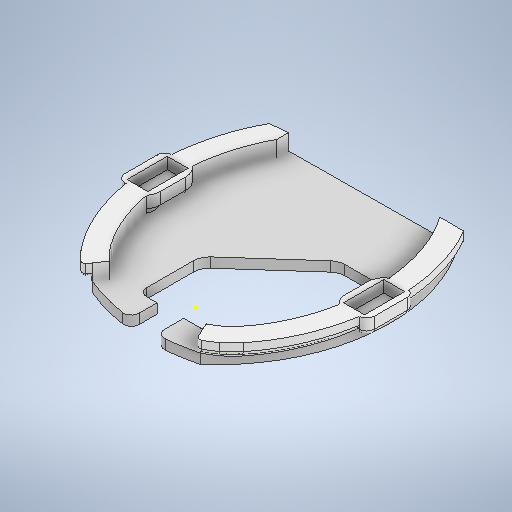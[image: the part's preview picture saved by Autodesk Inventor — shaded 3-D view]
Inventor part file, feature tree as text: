
AUTODESK INVENTOR PART (.ipt)
format: ipt  version: 2025.2 (Build 292293000, 293)  size: 827,392 bytes
history: native  units: in
note: dims shown in document units (in); Inventor stores cm internally (conversion verified against a paired STEP export)
features: fillet x10, sketch x6, extrude x5, other x3
ambient origin geometry x8: Origin, YZ Plane, XZ Plane, XY Plane, X Axis, Y Axis, Z Axis, Center Point
bodies: Solid1 (feature_tree), Solid2 (feature_tree)
feature tree (24):
  other  "rat_cap_EC_v12.iam"
  other  "rat_cap_walls_v8.iam:1::rat_cap_left_wall_v8.ipt:1"
  other  "rat_cap_walls_v8.iam:1::rat_cap_right_wall_v8.ipt:1"
  extrude  "Extrusion1"  Depth=0.3937in TaperAngle=0.0deg
  sketch  "Sketch3"  dims[d16=0.315in d17=0.0812in d18=0.0in]
  extrude  "Extrusion4"  Depth=0.0812in TaperAngle=0.0deg
  extrude  "Extrusion5"  Depth=0.2047in
  extrude  "Extrusion13"  Depth=0.2047in TaperAngle=0.0deg
  fillet  "Fillet7"  Radius=0.0787in
  fillet  "Fillet8"  Radius=0.0787in
  fillet  "Fillet9"  Radius=0.0394in
  fillet  "Fillet12"  Radius=0.0394in
  extrude  "Extrusion14"  Depth=0.0157in
  fillet  "Fillet13"  Radius=0.0394in
  fillet  "Fillet14"  Radius=0.0157in
  fillet  "Fillet15"  Radius=0.0157in
  fillet  "Fillet16"  Radius=0.0157in
  fillet  "Fillet17"  Radius=0.0157in
  fillet  "Fillet18"  Radius=0.0197in
  sketch  "Sketch1"  dims[d0=0.3937in d1=0.05in d2=0.0in]
  sketch  "Sketch5"  dims[d19=0.0591in d20=0.0in d44=0.2047in]
  sketch  "Sketch6"  dims[d45=0.2047in d46=0.0394in d47=0.0in d48=0.0787in d49=0.0787in d50=0.0394in d53=0.0394in]
  sketch  "Sketch14"  dims[d54=0.3937in d55=0.0in d56=0.0394in d57=0.0394in d58=0.0157in d59=0.0157in d60=0.0157in d61=0.0157in d33=0.0197in]
  sketch  "Sketch15"  dims[d34=0.0344in d35=0.0197in d36=0.0344in]
